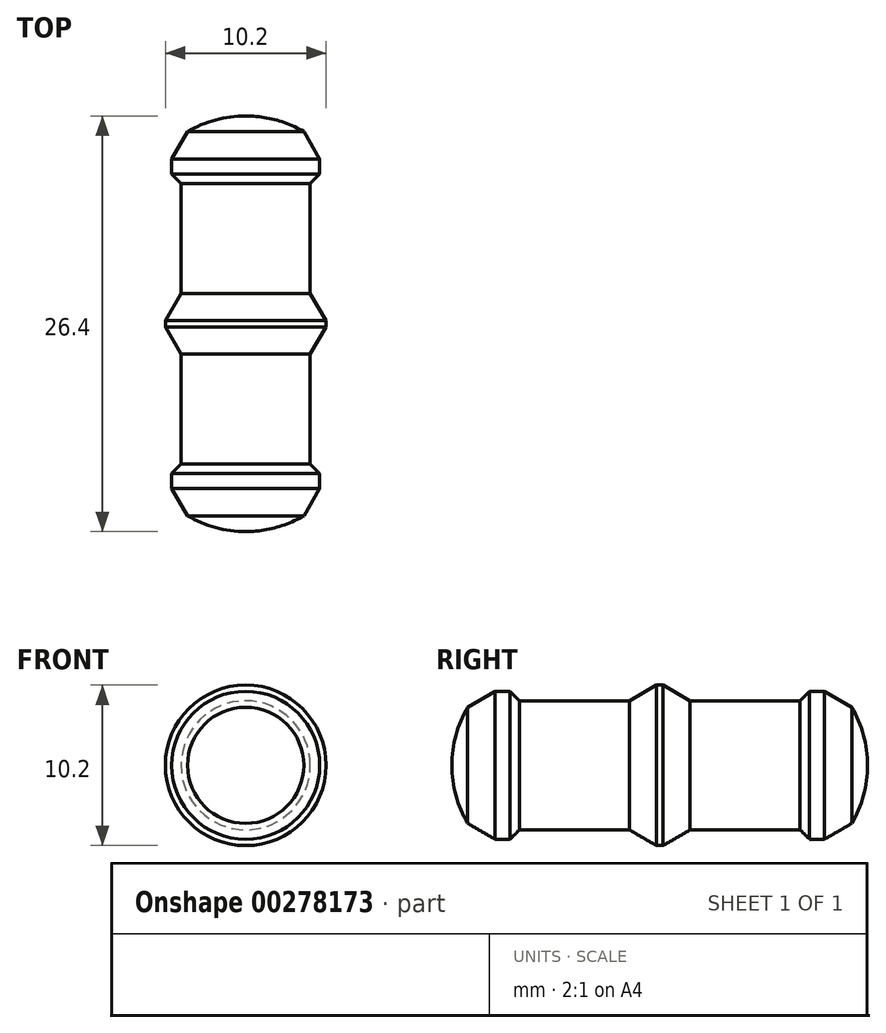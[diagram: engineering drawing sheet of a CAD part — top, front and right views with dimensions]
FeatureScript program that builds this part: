
annotation { "Feature Type Name" : "Feature", "Feature Type Description" : "" }
export const myFeature = defineFeature(function(context is Context, id is Id, definition is map)
    precondition{}
    {
        {
            var Q0;
            Q0=qCreatedBy(makeId("Top.planeOp"),FACE);
            var sketch = newSketch(context, id + "F0", { "sketchPlane" : qUnion([Q0])});
            skLineSegment(sketch, "E0", {"start": v(-4.5, 10.4) * mm, "end": v(-3.58, 12) * mm});
            skLineSegment(sketch, "E1", {"start": v(0, 0) * mm, "end": v(-3.9, 0) * mm});
            skLineSegment(sketch, "E2", {"start": v(-3.9, 0) * mm, "end": v(-3.9, 9) * mm});
            skLineSegment(sketch, "E3", {"start": v(-3.9, 9) * mm, "end": v(-4.5, 9.6) * mm});
            skLineSegment(sketch, "E4", {"start": v(-4.5, 9.6) * mm, "end": v(-4.5, 10.4) * mm});
            skLineSegment(sketch, "E5", {"start": v(-1.5, 12) * mm, "end": v(-1.5, 4) * mm});
            skArc(sketch, "E6", {"start": v(-1.5, 4) * mm, "mid": v(-1.06, 2.94) * mm, "end": v(0, 2.5) * mm});
            skLineSegment(sketch, "E7.trimOffspring", {"start": v(0, 2.5) * mm, "end": v(0, 0) * mm});
            skLineSegment(sketch, "E8", {"start": v(0, 2.5) * mm, "end": v(0, 12) * mm});
            skLineSegment(sketch, "E9", {"start": v(-3.58, 12) * mm, "end": v(0, 12) * mm});
            skLineSegment(sketch, "E10", {"start": v(0, 0) * mm, "end": v(0, -3.9) * mm, "construction": true});
            skLineSegment(sketch, "E11", {"start": v(0, 12) * mm, "end": v(0, 15.9) * mm, "construction": true});
            skSolve(sketch);
        }
        {
            var Q0;
            Q0=qCreatedBy(makeId("Right.planeOp"),FACE);
            var sketch = newSketch(context, id + "F1", { "sketchPlane" : qUnion([Q0])});
            skLineSegment(sketch, "E12.bottom", {"start": v(0, 4.5) * mm, "end": v(12, 4.5) * mm});
            skLineSegment(sketch, "E12.top", {"start": v(0, 2.9) * mm, "end": v(12, 2.9) * mm});
            skLineSegment(sketch, "E12.left", {"start": v(0, 4.5) * mm, "end": v(0, 2.9) * mm});
            skLineSegment(sketch, "E12.right", {"start": v(12, 4.5) * mm, "end": v(12, 2.9) * mm});
            skLineSegment(sketch, "E13.bottom", {"start": v(0, -2.9) * mm, "end": v(12, -2.9) * mm});
            skLineSegment(sketch, "E13.top", {"start": v(0, -4.5) * mm, "end": v(12, -4.5) * mm});
            skLineSegment(sketch, "E13.left", {"start": v(0, -2.9) * mm, "end": v(0, -4.5) * mm});
            skLineSegment(sketch, "E13.right", {"start": v(12, -2.9) * mm, "end": v(12, -4.5) * mm});
            skSolve(sketch);
        }
        {
            var Q0;
            Q0=qCreatedBy(makeId("Top.planeOp"),FACE);
            var sketch = newSketch(context, id + "F2", { "sketchPlane" : qUnion([Q0])});
            skLineSegment(sketch, "E14", {"start": v(-4.1, 1.93) * mm, "end": v(-5.1, 0.2) * mm});
            skLineSegment(sketch, "E15", {"start": v(-5.1, 0.2) * mm, "end": v(-5.1, 0) * mm});
            skLineSegment(sketch, "E16", {"start": v(-5.1, 0) * mm, "end": v(0, 0) * mm});
            skLineSegment(sketch, "E17", {"start": v(0, 0) * mm, "end": v(0, 13.2) * mm});
            skArc(sketch, "E18", {"start": v(0, 13.2) * mm, "mid": v(-1.91, 12.95) * mm, "end": v(-3.7, 12.2) * mm});
            skLineSegment(sketch, "E19.0", {"start": v(-3.7, 12.2) * mm, "end": v(0, 12.2) * mm, "construction": true});
            skLineSegment(sketch, "E19.1", {"start": v(-4.1, 1.93) * mm, "end": v(-4.1, 8.92) * mm});
            skLineSegment(sketch, "E19.2", {"start": v(-4.1, 8.92) * mm, "end": v(-4.7, 9.52) * mm});
            skLineSegment(sketch, "E19.3", {"start": v(-4.7, 9.52) * mm, "end": v(-4.7, 10.45) * mm});
            skLineSegment(sketch, "E19.4", {"start": v(-4.7, 10.45) * mm, "end": v(-3.7, 12.2) * mm});
            skSolve(sketch);
        }
        {
            var Q0;
            Q0=makeQuery(id+"F0.imprint","IMPRINT",FACE,{"disambiguationData":[TD([[makeQuery(id+"F0.imprint","IMPRINT",EDGE,{"derivedFrom":sQuery(id+"F0.wireOp",EDGE,"E0")}),-1.0]])]});
            var Q1;
            Q1=sQuery(id+"F0.wireOp",EDGE,"E8");
            revolve(context, id + "F3", {"entities" : qUnion([Q0]), "axis" : qUnion([Q1]), "revolveType" : RevolveType.SYMMETRIC, "angle" : 180 * degree});
        }
        {
            var Q0;
            {var subQ0=sQuery(id+"F0.wireOp",EDGE,"E5");Q0=makeQuery(id+"F0.imprint","IMPRINT",FACE,{"disambiguationData":[TD([[makeQuery(id+"F0.imprint","IMPRINT",EDGE,{"derivedFrom":subQ0}),1.0]])]});}
            extrude(context, id + "F4", {"entities" : qUnion([Q0]), "operationType" : NewBodyOperationType.REMOVE, "endBound" : BoundingType.THROUGH_ALL, "depth" : 25 * mm, "hasSecondDirection" : true, "secondDirectionBound" : BoundingType.THROUGH_ALL, "secondDirectionOppositeDirection" : true, "secondDirectionDepth" : 25 * mm});
        }
        {
            var Q0;
            Q0=makeQuery(id+"F1.imprint","IMPRINT",FACE,{"disambiguationData":[TD([[makeQuery(id+"F1.imprint","IMPRINT",EDGE,{"derivedFrom":sQuery(id+"F1.wireOp",EDGE,"E12.bottom")}),-1.0]])]});
            var Q1;
            Q1=makeQuery(id+"F1.imprint","IMPRINT",FACE,{"disambiguationData":[TD([[makeQuery(id+"F1.imprint","IMPRINT",EDGE,{"derivedFrom":sQuery(id+"F1.wireOp",EDGE,"E13.bottom")}),-1.0]])]});
            extrude(context, id + "F5", {"entities" : qUnion([Q0, Q1]), "operationType" : NewBodyOperationType.REMOVE, "endBound" : BoundingType.THROUGH_ALL, "oppositeDirection" : true, "depth" : 25 * mm});
        }
        {
            var Q0;
            Q0=makeQuery(id+"F3.opRevolve","SWEPT_BODY",BODY,{"disambiguationData":[OSD([sQuery(id+"F0.wireOp",EDGE,"E0"),sQuery(id+"F0.wireOp",EDGE,"E1"),sQuery(id+"F0.wireOp",EDGE,"E2"),sQuery(id+"F0.wireOp",EDGE,"E3"),sQuery(id+"F0.wireOp",EDGE,"E4"),sQuery(id+"F0.wireOp",EDGE,"E5"),sQuery(id+"F0.wireOp",EDGE,"E6"),sQuery(id+"F0.wireOp",EDGE,"E7.trimOffspring"),sQuery(id+"F0.wireOp",EDGE,"E9")])]});
            var Q1;
            Q1=qCreatedBy(makeId("Right.planeOp"),FACE);
            mirror(context, id + "F6", {"operationType" : NewBodyOperationType.ADD, "entities" : qUnion([Q0]), "mirrorPlane" : qUnion([Q1])});
        }
        {
            var Q0;
            Q0=makeQuery(id+"F3.opRevolve","SWEPT_BODY",BODY,{"disambiguationData":[OSD([sQuery(id+"F0.wireOp",EDGE,"E0"),sQuery(id+"F0.wireOp",EDGE,"E1"),sQuery(id+"F0.wireOp",EDGE,"E2"),sQuery(id+"F0.wireOp",EDGE,"E3"),sQuery(id+"F0.wireOp",EDGE,"E4"),sQuery(id+"F0.wireOp",EDGE,"E5"),sQuery(id+"F0.wireOp",EDGE,"E6"),sQuery(id+"F0.wireOp",EDGE,"E7.trimOffspring"),sQuery(id+"F0.wireOp",EDGE,"E9")])]});
            var Q1;
            Q1=qCreatedBy(makeId("Front.planeOp"),FACE);
            mirror(context, id + "F7", {"operationType" : NewBodyOperationType.ADD, "entities" : qUnion([Q0]), "mirrorPlane" : qUnion([Q1])});
        }
        {
            var Q0;
            Q0=makeQuery(id+"F2.imprint","IMPRINT",FACE,{"disambiguationData":[TD([[makeQuery(id+"F2.imprint","IMPRINT",EDGE,{"derivedFrom":sQuery(id+"F2.wireOp",EDGE,"E14")}),1.0]])]});
            var Q1;
            Q1=sQuery(id+"F2.wireOp",EDGE,"E17");
            revolve(context, id + "F8", {"entities" : qUnion([Q0]), "axis" : qUnion([Q1]), "revolveType" : RevolveType.FULL});
        }
        {
            var Q0;
            Q0=makeQuery(id+"F8.opRevolve","SWEPT_BODY",BODY,{"disambiguationData":[OSD([sQuery(id+"F2.wireOp",EDGE,"E14"),sQuery(id+"F2.wireOp",EDGE,"E15"),sQuery(id+"F2.wireOp",EDGE,"E16"),sQuery(id+"F2.wireOp",EDGE,"E17"),sQuery(id+"F2.wireOp",EDGE,"E18"),sQuery(id+"F2.wireOp",EDGE,"3236d3ef-0a48-433c-8bb1-e87a61540549"),sQuery(id+"F2.wireOp",EDGE,"E19.1"),sQuery(id+"F2.wireOp",EDGE,"E19.2"),sQuery(id+"F2.wireOp",EDGE,"E19.3"),sQuery(id+"F2.wireOp",EDGE,"E19.4")])]});
            var Q1;
            Q1=qCreatedBy(makeId("Front.planeOp"),FACE);
            mirror(context, id + "F9", {"operationType" : NewBodyOperationType.ADD, "entities" : qUnion([Q0]), "mirrorPlane" : qUnion([Q1])});
        }
    });
